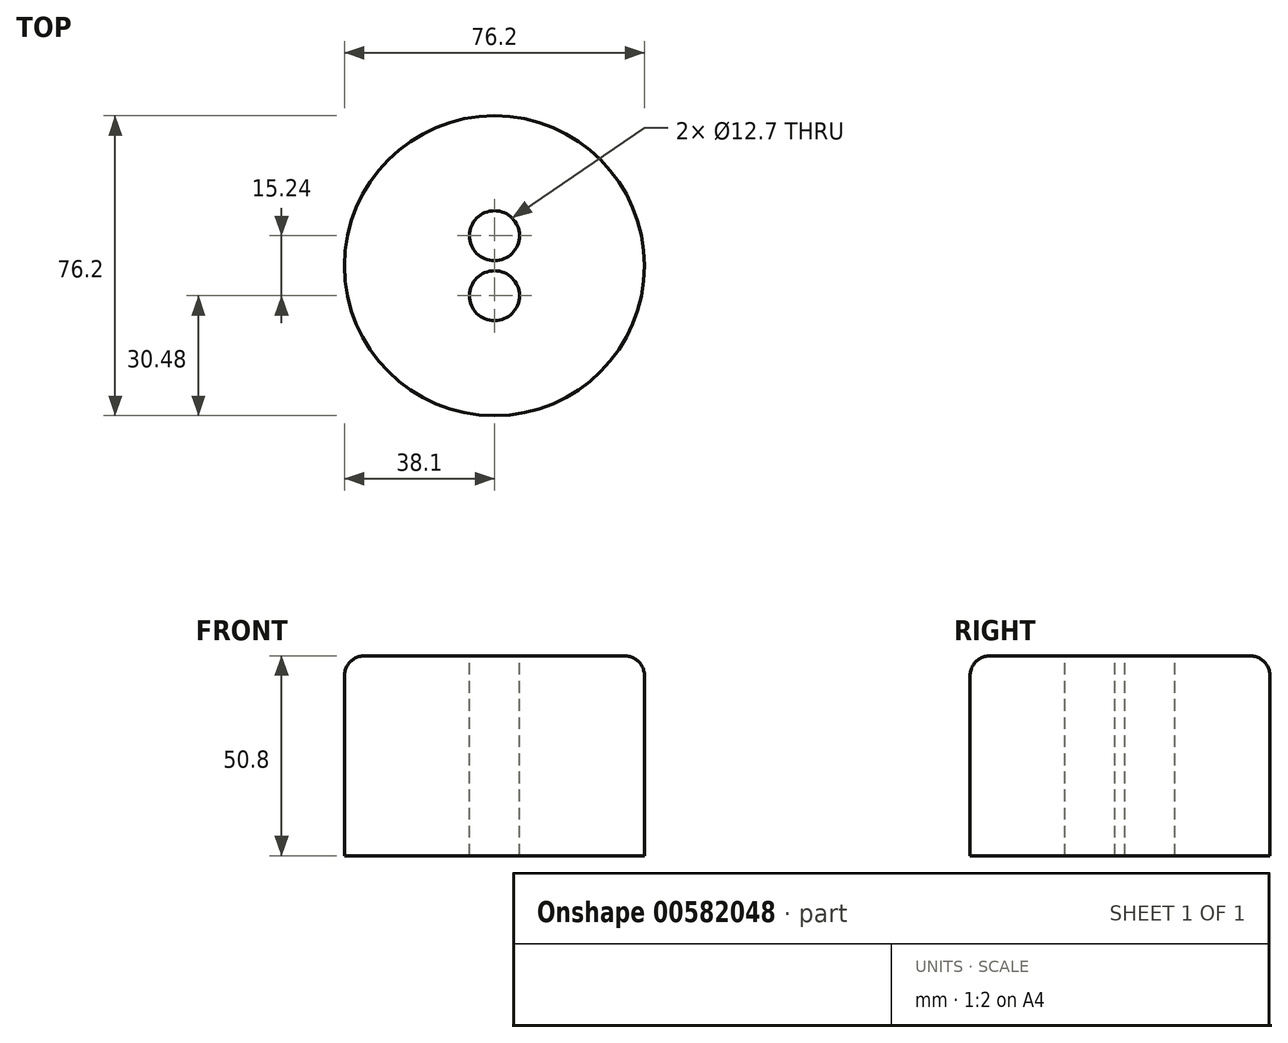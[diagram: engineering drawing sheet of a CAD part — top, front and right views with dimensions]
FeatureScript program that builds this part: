
annotation { "Feature Type Name" : "Feature", "Feature Type Description" : "" }
export const myFeature = defineFeature(function(context is Context, id is Id, definition is map)
    precondition{}
    {
        {
            var Q0;
            Q0=qCreatedBy(makeId("Top.planeOp"),FACE);
            var sketch = newSketch(context, id + "F0", { "sketchPlane" : qUnion([Q0])});
            skCircle(sketch, "E0", {"center": v(0, 0) * mm, "radius": 38.1 * mm});
            skSolve(sketch);
        }
        {
            var Q0;
            Q0=makeQuery(id+"F0.imprint","IMPRINT",FACE,{"disambiguationData":[TD([[makeQuery(id+"F0.imprint","IMPRINT",EDGE,{"derivedFrom":sQuery(id+"F0.wireOp",EDGE,"E0")}),1.0]])]});
            extrude(context, id + "F1", {"entities" : qUnion([Q0]), "depth" : 50.8 * mm, "offsetDistance" : 25.4 * mm});
        }
        {
            var Q0;
            Q0=makeQuery(id+"F1.opExtrude","CAP_FACE",FACE,{"disambiguationData":[OSD([sQuery(id+"F0.wireOp",EDGE,"E0")])],"isStart":false});
            var sketch = newSketch(context, id + "F2", { "sketchPlane" : qUnion([Q0])});
            skCircle(sketch, "E1", {"center": v(0, 7.62) * mm, "radius": 6.35 * mm});
            skCircle(sketch, "E2", {"center": v(0, -7.62) * mm, "radius": 6.35 * mm});
            skSolve(sketch);
        }
        {
            var Q0;
            Q0=makeQuery(id+"F2.imprint","IMPRINT",FACE,{"disambiguationData":[TD([[makeQuery(id+"F2.imprint","IMPRINT",EDGE,{"derivedFrom":sQuery(id+"F2.wireOp",EDGE,"E1")}),1.0]])]});
            var Q1;
            Q1=makeQuery(id+"F2.imprint","IMPRINT",FACE,{"disambiguationData":[TD([[makeQuery(id+"F2.imprint","IMPRINT",EDGE,{"derivedFrom":sQuery(id+"F2.wireOp",EDGE,"E2")}),1.0]])]});
            extrude(context, id + "F3", {"entities" : qUnion([Q0, Q1]), "operationType" : NewBodyOperationType.REMOVE, "oppositeDirection" : true, "depth" : 70.61 * mm, "offsetDistance" : 25.4 * mm});
        }
        {
            var Q0;
            Q0=makeQuery(id+"F1.opExtrude","CAP_EDGE",EDGE,{"disambiguationData":[OSD([sQuery(id+"F0.wireOp",EDGE,"E0")])],"isStart":false});
            fillet(context, id + "F4", {"entities" : qUnion([Q0]), "radius" : 5.08 * mm, "tangentPropagation" : true, "allowEdgeOverflow" : false});
        }
    });
